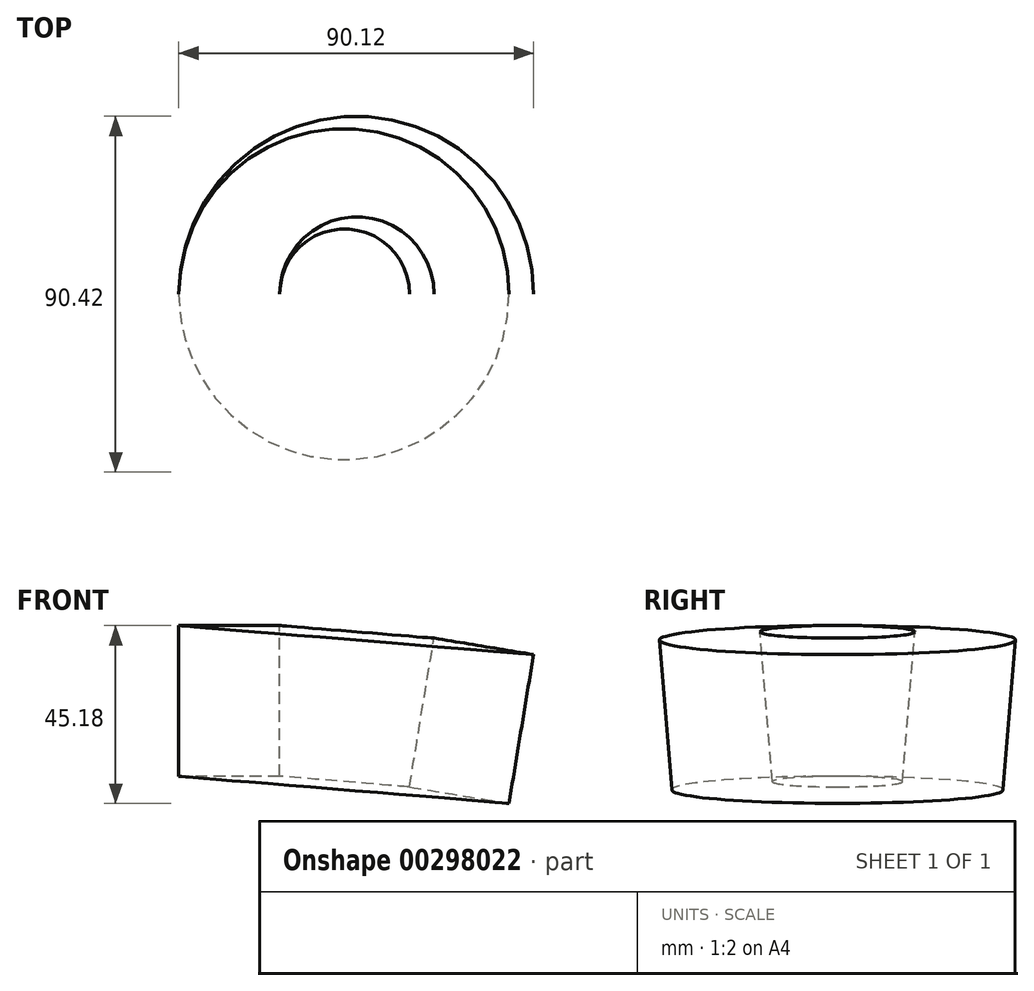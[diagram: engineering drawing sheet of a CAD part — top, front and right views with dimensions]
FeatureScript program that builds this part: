
annotation { "Feature Type Name" : "Feature", "Feature Type Description" : "" }
export const myFeature = defineFeature(function(context is Context, id is Id, definition is map)
    precondition{}
    {
        {
            var Q0;
            Q0=qCreatedBy(makeId("Front.planeOp"),FACE);
            var sketch = newSketch(context, id + "F0", { "sketchPlane" : qUnion([Q0])});
            skLineSegment(sketch, "E0.bottom", {"start": v(0, 0) * mm, "end": v(-25.63, 0) * mm});
            skLineSegment(sketch, "E0.top", {"start": v(0, -38.31) * mm, "end": v(-25.63, -38.31) * mm});
            skLineSegment(sketch, "E0.left", {"start": v(0, 0) * mm, "end": v(0, -38.31) * mm});
            skLineSegment(sketch, "E0.right", {"start": v(-25.63, 0) * mm, "end": v(-25.63, -38.31) * mm});
            skLineSegment(sketch, "E1", {"start": v(20.5, 9.46) * mm, "end": v(16.23, -42.7) * mm});
            skSolve(sketch);
        }
        {
            var Q0;
            Q0=makeQuery(id+"F0.imprint","IMPRINT",FACE,{"disambiguationData":[TD([[makeQuery(id+"F0.imprint","IMPRINT",EDGE,{"derivedFrom":sQuery(id+"F0.wireOp",EDGE,"E0.bottom")}),1.0]])]});
            var Q1;
            Q1=sQuery(id+"F0.wireOp",EDGE,"E1");
            var Q2;
            Q2=sQuery(id+"F0.wireOp",EDGE,"E1");
            revolve(context, id + "F1", {"entities" : qUnion([Q0]), "surfaceEntities" : qUnion([Q1]), "axis" : qUnion([Q2]), "revolveType" : RevolveType.FULL});
        }
    });
